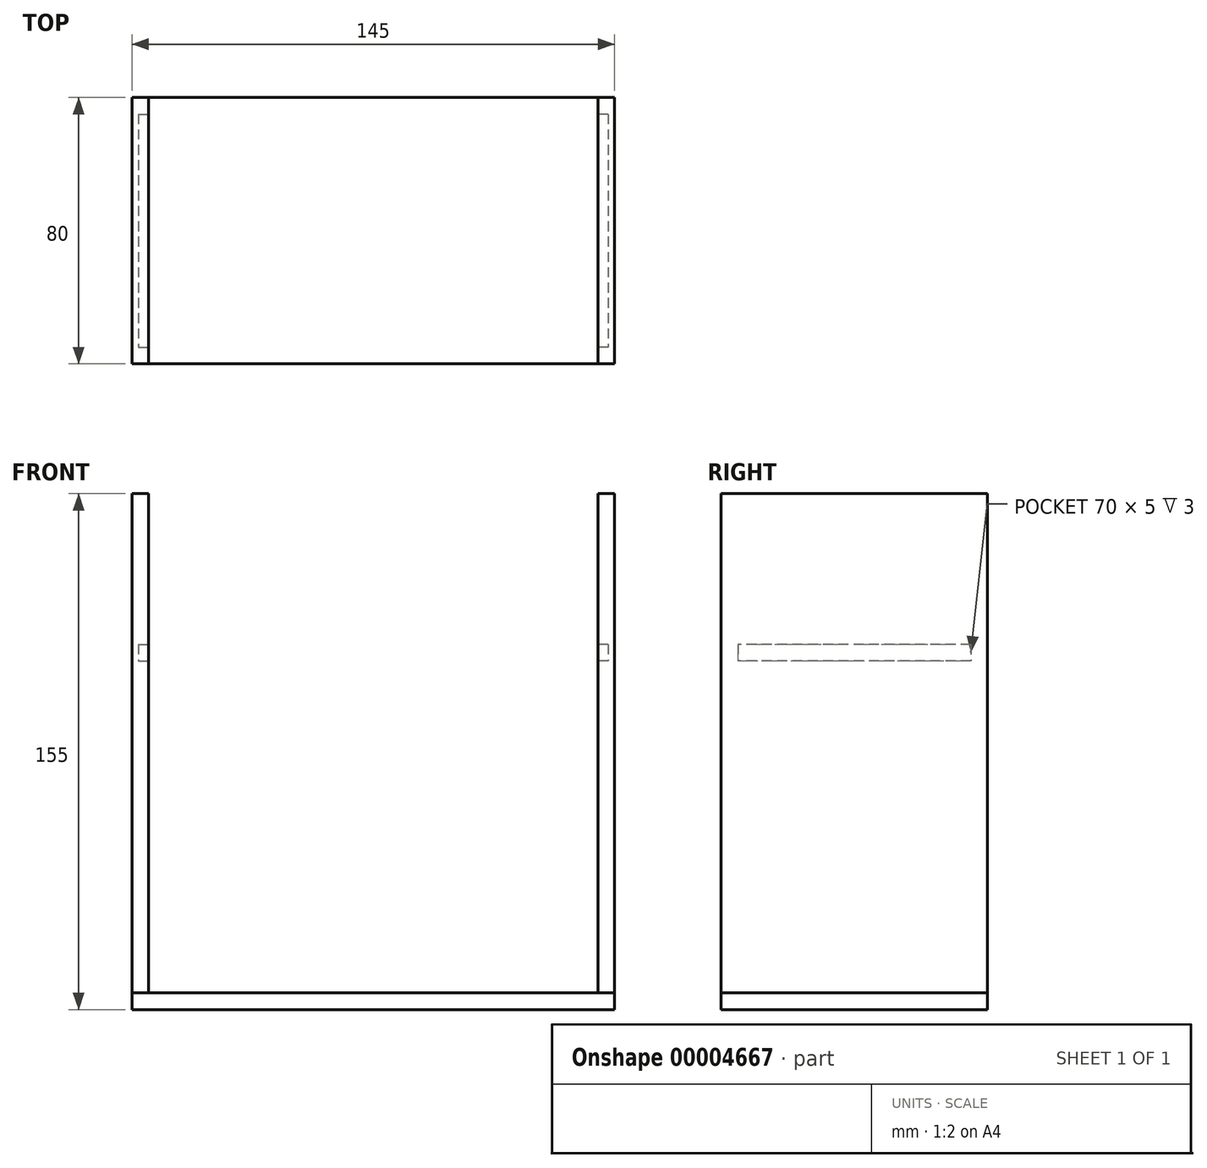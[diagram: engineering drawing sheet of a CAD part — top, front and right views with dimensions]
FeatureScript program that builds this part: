
annotation { "Feature Type Name" : "Feature", "Feature Type Description" : "" }
export const myFeature = defineFeature(function(context is Context, id is Id, definition is map)
    precondition{}
    {
        {
            var Q0;
            Q0=qCreatedBy(makeId("Top.planeOp"),FACE);
            var sketch = newSketch(context, id + "F0", { "sketchPlane" : qUnion([Q0])});
            skLineSegment(sketch, "E0.rect.bottom", {"start": v(72.5, 40) * mm, "end": v(-72.5, 40) * mm});
            skLineSegment(sketch, "E0.rect.top", {"start": v(72.5, -40) * mm, "end": v(-72.5, -40) * mm});
            skLineSegment(sketch, "E0.rect.left", {"start": v(72.5, 40) * mm, "end": v(72.5, -40) * mm});
            skLineSegment(sketch, "E0.rect.right", {"start": v(-72.5, 40) * mm, "end": v(-72.5, -40) * mm});
            skPoint(sketch, "E0.rect.middle", {"position": v(0, 0) * mm});
            skSolve(sketch);
        }
        {
            var Q0;
            Q0 = qSketchRegion(id + "F0", true);
            extrude(context, id + "F1", {"entities" : qUnion([Q0]), "depth" : 5 * mm});
        }
        {
            var Q0;
            Q0=makeQuery(id+"F1.opExtrude","CAP_FACE",FACE,{"disambiguationData":[OSD([sQuery(id+"F0.wireOp",EDGE,"E0.rect.bottom"),sQuery(id+"F0.wireOp",EDGE,"E0.rect.top"),sQuery(id+"F0.wireOp",EDGE,"E0.rect.left"),sQuery(id+"F0.wireOp",EDGE,"E0.rect.right")])],"isStart":false});
            var sketch = newSketch(context, id + "F2", { "sketchPlane" : qUnion([Q0])});
            skLineSegment(sketch, "E1.bottom", {"start": v(-72.5, -40) * mm, "end": v(-67.5, -40) * mm});
            skLineSegment(sketch, "E1.top", {"start": v(-72.5, 40) * mm, "end": v(-67.5, 40) * mm});
            skLineSegment(sketch, "E1.left", {"start": v(-72.5, -40) * mm, "end": v(-72.5, 40) * mm});
            skLineSegment(sketch, "E1.right", {"start": v(-67.5, -40) * mm, "end": v(-67.5, 40) * mm});
            skSolve(sketch);
        }
        {
            var Q0;
            Q0 = qSketchRegion(id + "F2", true);
            extrude(context, id + "F3", {"entities" : qUnion([Q0]), "operationType" : NewBodyOperationType.ADD, "depth" : 150 * mm});
        }
        {
            var Q0;
            Q0=makeQuery(id+"F1.opExtrude","SWEPT_BODY",BODY,{"disambiguationData":[OSD([sQuery(id+"F0.wireOp",EDGE,"E0.rect.bottom"),sQuery(id+"F0.wireOp",EDGE,"E0.rect.top"),sQuery(id+"F0.wireOp",EDGE,"E0.rect.left"),sQuery(id+"F0.wireOp",EDGE,"E0.rect.right")])]});
            var Q1;
            Q1=qCreatedBy(makeId("Right.planeOp"),FACE);
            mirror(context, id + "F4", {"entities" : qUnion([Q0]), "mirrorPlane" : qUnion([Q1])});
        }
        {
            var Q0;
            Q0=makeQuery(id+"F3.opExtrude","SWEPT_FACE",FACE,{"disambiguationData":[OSD([sQuery(id+"F2.wireOp",EDGE,"E1.right")])]});
            var sketch = newSketch(context, id + "F5", { "sketchPlane" : qUnion([Q0])});
            skLineSegment(sketch, "E2.rect.bottom", {"start": v(35, 109.73) * mm, "end": v(-35, 109.73) * mm});
            skLineSegment(sketch, "E2.rect.top", {"start": v(35, 104.73) * mm, "end": v(-35, 104.73) * mm});
            skLineSegment(sketch, "E2.rect.left", {"start": v(35, 109.73) * mm, "end": v(35, 104.73) * mm});
            skLineSegment(sketch, "E2.rect.right", {"start": v(-35, 109.73) * mm, "end": v(-35, 104.73) * mm});
            skPoint(sketch, "E2.rect.middle", {"position": v(0, 107.23) * mm});
            skSolve(sketch);
        }
        {
            var Q0;
            Q0 = qSketchRegion(id + "F5", true);
            extrude(context, id + "F6", {"entities" : qUnion([Q0]), "operationType" : NewBodyOperationType.REMOVE, "oppositeDirection" : true, "depth" : 3 * mm});
        }
        {
            var Q0;
            Q0=makeQuery(id+"F4.opPattern","COPY",BODY,{"derivedFrom":makeQuery(id+"F1.opExtrude","SWEPT_BODY",BODY,{"disambiguationData":[OSD([sQuery(id+"F0.wireOp",EDGE,"E0.rect.bottom"),sQuery(id+"F0.wireOp",EDGE,"E0.rect.top"),sQuery(id+"F0.wireOp",EDGE,"E0.rect.left"),sQuery(id+"F0.wireOp",EDGE,"E0.rect.right")])]}),"instanceName":"1"});
            deleteBodies(context, id + "F7", {"entities" : qUnion([Q0])});
        }
        {
            var Q0;
            Q0=makeQuery(id+"F1.opExtrude","SWEPT_BODY",BODY,{"disambiguationData":[OSD([sQuery(id+"F0.wireOp",EDGE,"E0.rect.bottom"),sQuery(id+"F0.wireOp",EDGE,"E0.rect.top"),sQuery(id+"F0.wireOp",EDGE,"E0.rect.left"),sQuery(id+"F0.wireOp",EDGE,"E0.rect.right")])]});
            var Q1;
            Q1=qCreatedBy(makeId("Right.planeOp"),FACE);
            mirror(context, id + "F8", {"entities" : qUnion([Q0]), "mirrorPlane" : qUnion([Q1])});
        }
    });
